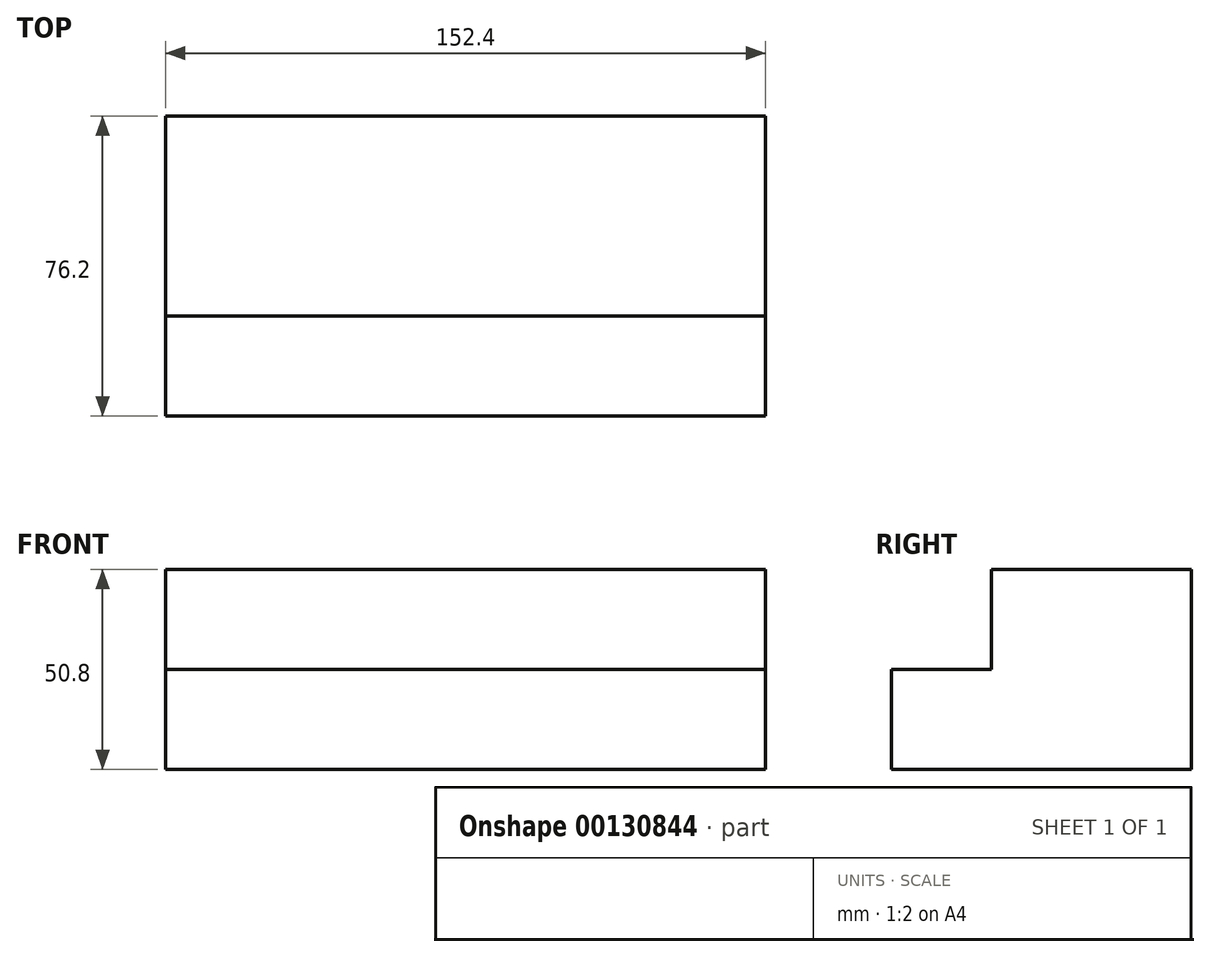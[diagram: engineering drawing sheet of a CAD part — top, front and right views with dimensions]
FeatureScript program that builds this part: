
annotation { "Feature Type Name" : "Feature", "Feature Type Description" : "" }
export const myFeature = defineFeature(function(context is Context, id is Id, definition is map)
    precondition{}
    {
        {
            var Q0;
            Q0=qCreatedBy(makeId("Right.planeOp"),FACE);
            var sketch = newSketch(context, id + "F0", { "sketchPlane" : qUnion([Q0])});
            skLineSegment(sketch, "E0", {"start": v(-35.1, -10.26) * mm, "end": v(41.1, -10.26) * mm});
            skLineSegment(sketch, "E1", {"start": v(41.1, -10.26) * mm, "end": v(41.1, 40.54) * mm});
            skLineSegment(sketch, "E2", {"start": v(41.1, 40.54) * mm, "end": v(-9.7, 40.54) * mm});
            skLineSegment(sketch, "E3", {"start": v(-9.7, 40.54) * mm, "end": v(-9.7, 15.14) * mm});
            skLineSegment(sketch, "E4", {"start": v(-9.7, 15.14) * mm, "end": v(-35.1, 15.14) * mm});
            skLineSegment(sketch, "E5", {"start": v(-35.1, 15.14) * mm, "end": v(-35.1, -10.26) * mm});
            skSolve(sketch);
        }
        {
            var Q0;
            Q0 = qSketchRegion(id + "F0", true);
            extrude(context, id + "F1", {"entities" : qUnion([Q0]), "endBound" : BoundingType.SYMMETRIC, "depth" : 152.4 * mm});
        }
    });
